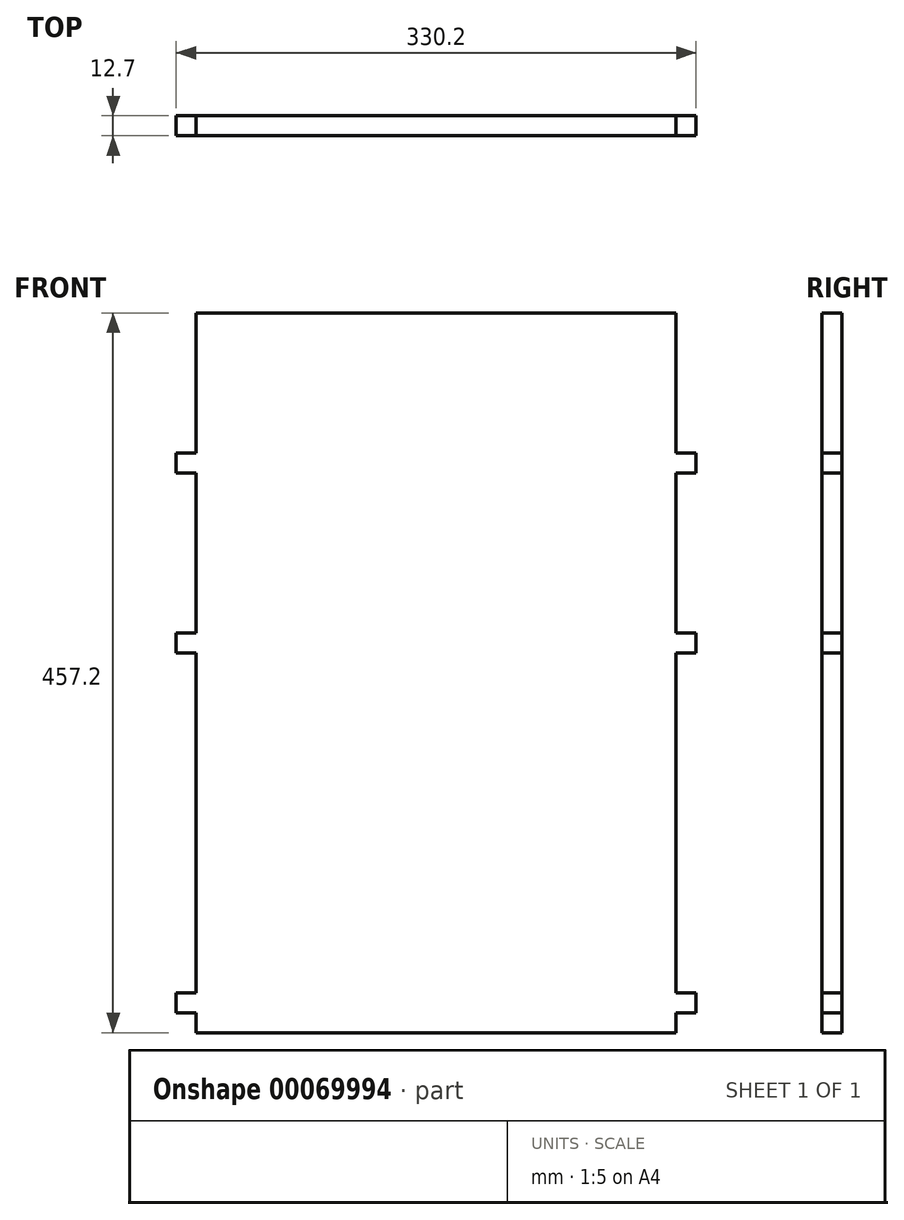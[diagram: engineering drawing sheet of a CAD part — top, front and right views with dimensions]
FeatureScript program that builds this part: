
annotation { "Feature Type Name" : "Feature", "Feature Type Description" : "" }
export const myFeature = defineFeature(function(context is Context, id is Id, definition is map)
    precondition{}
    {
        {
            var Q0;
            Q0=qCreatedBy(makeId("Front.planeOp"),FACE);
            var sketch = newSketch(context, id + "F0", { "sketchPlane" : qUnion([Q0])});
            skLineSegment(sketch, "E0.rect.bottom", {"start": v(152.4, 228.6) * mm, "end": v(-152.4, 228.6) * mm});
            skLineSegment(sketch, "E0.rect.top", {"start": v(152.4, -228.6) * mm, "end": v(-152.4, -228.6) * mm});
            skLineSegment(sketch, "E0.rect.left", {"start": v(152.4, 228.6) * mm, "end": v(152.4, -228.6) * mm});
            skLineSegment(sketch, "E0.rect.right", {"start": v(-152.4, 228.6) * mm, "end": v(-152.4, -228.6) * mm});
            skPoint(sketch, "E0.rect.middle", {"position": v(0, 0) * mm});
            skLineSegment(sketch, "E1.bottom", {"start": v(-152.4, 139.7) * mm, "end": v(-165.1, 139.7) * mm});
            skLineSegment(sketch, "E1.top", {"start": v(-152.4, 127) * mm, "end": v(-165.1, 127) * mm});
            skLineSegment(sketch, "E1.left", {"start": v(-152.4, 139.7) * mm, "end": v(-152.4, 127) * mm});
            skLineSegment(sketch, "E1.right", {"start": v(-165.1, 139.7) * mm, "end": v(-165.1, 127) * mm});
            skLineSegment(sketch, "E2.bottom", {"start": v(-152.4, 25.4) * mm, "end": v(-165.1, 25.4) * mm});
            skLineSegment(sketch, "E2.top", {"start": v(-152.4, 12.7) * mm, "end": v(-165.1, 12.7) * mm});
            skLineSegment(sketch, "E2.left", {"start": v(-152.4, 25.4) * mm, "end": v(-152.4, 12.7) * mm});
            skLineSegment(sketch, "E2.right", {"start": v(-165.1, 25.4) * mm, "end": v(-165.1, 12.7) * mm});
            skLineSegment(sketch, "E3.bottom", {"start": v(-152.4, -203.2) * mm, "end": v(-165.1, -203.2) * mm});
            skLineSegment(sketch, "E3.top", {"start": v(-152.4, -215.9) * mm, "end": v(-165.1, -215.9) * mm});
            skLineSegment(sketch, "E3.left", {"start": v(-152.4, -203.2) * mm, "end": v(-152.4, -215.9) * mm});
            skLineSegment(sketch, "E3.right", {"start": v(-165.1, -203.2) * mm, "end": v(-165.1, -215.9) * mm});
            skLineSegment(sketch, "E4", {"start": v(0, 228.6) * mm, "end": v(0, -228.6) * mm, "construction": true});
            skLineSegment(sketch, "E5.MirrorCS", {"start": v(152.4, -215.9) * mm, "end": v(165.1, -215.9) * mm});
            skLineSegment(sketch, "E6.MirrorCS", {"start": v(152.4, -203.2) * mm, "end": v(152.4, -215.9) * mm});
            skLineSegment(sketch, "E7.MirrorCS", {"start": v(152.4, -203.2) * mm, "end": v(165.1, -203.2) * mm});
            skLineSegment(sketch, "E8.MirrorCS", {"start": v(165.1, 25.4) * mm, "end": v(165.1, 12.7) * mm});
            skLineSegment(sketch, "E9.MirrorCS", {"start": v(152.4, 25.4) * mm, "end": v(152.4, 12.7) * mm});
            skLineSegment(sketch, "E10.MirrorCS", {"start": v(165.1, -203.2) * mm, "end": v(165.1, -215.9) * mm});
            skLineSegment(sketch, "E11.MirrorCS", {"start": v(152.4, 139.7) * mm, "end": v(165.1, 139.7) * mm});
            skLineSegment(sketch, "E12.MirrorCS", {"start": v(152.4, 127) * mm, "end": v(165.1, 127) * mm});
            skLineSegment(sketch, "E13.MirrorCS", {"start": v(152.4, 12.7) * mm, "end": v(165.1, 12.7) * mm});
            skLineSegment(sketch, "E14.MirrorCS", {"start": v(152.4, 139.7) * mm, "end": v(152.4, 127) * mm});
            skLineSegment(sketch, "E15.MirrorCS", {"start": v(152.4, 25.4) * mm, "end": v(165.1, 25.4) * mm});
            skLineSegment(sketch, "E16.MirrorCS", {"start": v(165.1, 139.7) * mm, "end": v(165.1, 127) * mm});
            skSolve(sketch);
        }
        {
            var Q0;
            {var subQ3=sQuery(id+"F0.wireOp",EDGE,"E0.rect.bottom");Q0=makeQuery(id+"F0.imprint","IMPRINT",FACE,{"disambiguationData":[TD([[makeQuery(id+"F0.imprint","IMPRINT",EDGE,{"derivedFrom":subQ3}),1.0]])]});}
            var Q1;
            Q1=makeQuery(id+"F0.imprint","IMPRINT",FACE,{"disambiguationData":[TD([[makeQuery(id+"F0.imprint","IMPRINT",EDGE,{"derivedFrom":sQuery(id+"F0.wireOp",EDGE,"E1.bottom")}),1.0]])]});
            var Q2;
            Q2=makeQuery(id+"F0.imprint","IMPRINT",FACE,{"disambiguationData":[TD([[makeQuery(id+"F0.imprint","IMPRINT",EDGE,{"derivedFrom":sQuery(id+"F0.wireOp",EDGE,"E2.bottom")}),1.0]])]});
            var Q3;
            Q3=makeQuery(id+"F0.imprint","IMPRINT",FACE,{"disambiguationData":[TD([[makeQuery(id+"F0.imprint","IMPRINT",EDGE,{"derivedFrom":sQuery(id+"F0.wireOp",EDGE,"E3.bottom")}),1.0]])]});
            var Q4;
            Q4=makeQuery(id+"F0.imprint","IMPRINT",FACE,{"disambiguationData":[TD([[makeQuery(id+"F0.imprint","IMPRINT",EDGE,{"derivedFrom":sQuery(id+"F0.wireOp",EDGE,"E5.MirrorCS")}),1.0]])]});
            var Q5;
            Q5=makeQuery(id+"F0.imprint","IMPRINT",FACE,{"disambiguationData":[TD([[makeQuery(id+"F0.imprint","IMPRINT",EDGE,{"derivedFrom":sQuery(id+"F0.wireOp",EDGE,"E8.MirrorCS")}),-1.0]])]});
            var Q6;
            Q6=makeQuery(id+"F0.imprint","IMPRINT",FACE,{"disambiguationData":[TD([[makeQuery(id+"F0.imprint","IMPRINT",EDGE,{"derivedFrom":sQuery(id+"F0.wireOp",EDGE,"E11.MirrorCS")}),-1.0]])]});
            extrude(context, id + "F1", {"entities" : qUnion([Q0, Q1, Q2, Q3, Q4, Q5, Q6]), "depth" : 12.7 * mm});
        }
    });
